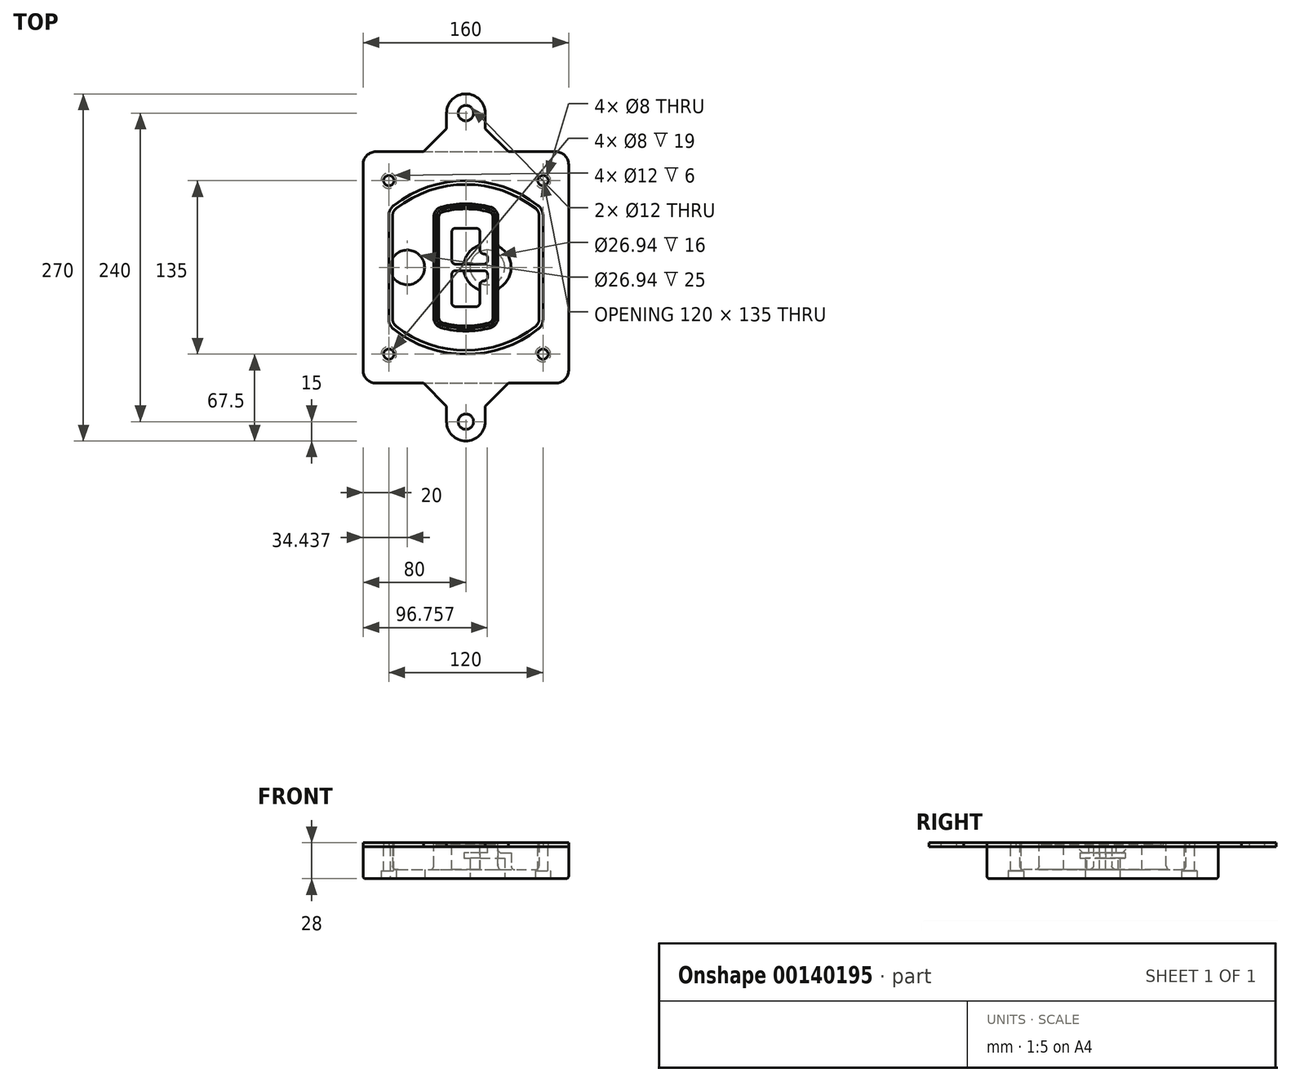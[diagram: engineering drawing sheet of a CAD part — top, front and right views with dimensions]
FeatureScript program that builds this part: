
annotation { "Feature Type Name" : "Feature", "Feature Type Description" : "" }
export const myFeature = defineFeature(function(context is Context, id is Id, definition is map)
    precondition{}
    {
        {
            var Q0;
            Q0=qCreatedBy(makeId("Top.planeOp"),FACE);
            var sketch = newSketch(context, id + "F0", { "sketchPlane" : qUnion([Q0])});
            skPoint(sketch, "E0.rect.middle", {"position": v(0, 0) * mm});
            skLineSegment(sketch, "E1.bottom", {"start": v(-70, -90) * mm, "end": v(70, -90) * mm});
            skLineSegment(sketch, "E1.top", {"start": v(-70, 90) * mm, "end": v(70, 90) * mm});
            skLineSegment(sketch, "E1.left", {"start": v(-80, -80) * mm, "end": v(-80, 80) * mm});
            skLineSegment(sketch, "E1.right", {"start": v(80, -80) * mm, "end": v(80, 80) * mm});
            skLineSegment(sketch, "E2", {"start": v(-80, 90) * mm, "end": v(80, -90) * mm, "construction": true});
            skLineSegment(sketch, "E3", {"start": v(80, 90) * mm, "end": v(-80, -90) * mm, "construction": true});
            skCircle(sketch, "E4", {"center": v(-60, 67.5) * mm, "radius": 4 * mm});
            skCircle(sketch, "E5", {"center": v(60, 67.5) * mm, "radius": 4 * mm});
            skCircle(sketch, "E6", {"center": v(60, -67.5) * mm, "radius": 4 * mm});
            skCircle(sketch, "E7", {"center": v(-60, -67.5) * mm, "radius": 4 * mm});
            skLineSegment(sketch, "E8", {"start": v(-60, 67.5) * mm, "end": v(60, 67.5) * mm, "construction": true});
            skLineSegment(sketch, "E9", {"start": v(60, 67.5) * mm, "end": v(60, -67.5) * mm, "construction": true});
            skLineSegment(sketch, "E10", {"start": v(60, -67.5) * mm, "end": v(-60, -67.5) * mm, "construction": true});
            skLineSegment(sketch, "E11", {"start": v(-60, -67.5) * mm, "end": v(-60, 67.5) * mm, "construction": true});
            skLineSegment(sketch, "E12", {"start": v(-60, 40.3) * mm, "end": v(-60, -40.3) * mm});
            skLineSegment(sketch, "E13", {"start": v(60, 40.3) * mm, "end": v(60, -40.3) * mm});
            skArc(sketch, "E14", {"start": v(56.15, 48.18) * mm, "mid": v(0, 67.5) * mm, "end": v(-56.15, 48.18) * mm});
            skArc(sketch, "E15", {"start": v(-56.15, -48.18) * mm, "mid": v(0, -67.5) * mm, "end": v(56.15, -48.18) * mm});
            skLineSegment(sketch, "E16", {"start": v(-60, 0) * mm, "end": v(60, 0) * mm, "construction": true});
            skPoint(sketch, "E17.visualSharp", {"position": v(-60, -45) * mm});
            skArc(sketch, "E17.filletArc", {"start": v(-60, -40.3) * mm, "mid": v(-58.99, -44.68) * mm, "end": v(-56.15, -48.18) * mm});
            skPoint(sketch, "E18.visualSharp", {"position": v(-60, 45) * mm});
            skArc(sketch, "E18.filletArc", {"start": v(-56.15, 48.18) * mm, "mid": v(-58.99, 44.68) * mm, "end": v(-60, 40.3) * mm});
            skPoint(sketch, "E19.visualSharp", {"position": v(60, 45) * mm});
            skArc(sketch, "E19.filletArc", {"start": v(60, 40.3) * mm, "mid": v(58.99, 44.68) * mm, "end": v(56.15, 48.18) * mm});
            skPoint(sketch, "E20.visualSharp", {"position": v(60, -45) * mm});
            skArc(sketch, "E20.filletArc", {"start": v(56.15, -48.18) * mm, "mid": v(58.99, -44.68) * mm, "end": v(60, -40.3) * mm});
            skPoint(sketch, "E21.visualSharp", {"position": v(-80, 90) * mm});
            skArc(sketch, "E21.filletArc", {"start": v(-70, 90) * mm, "mid": v(-77.07, 87.07) * mm, "end": v(-80, 80) * mm});
            skPoint(sketch, "E22.visualSharp", {"position": v(80, 90) * mm});
            skArc(sketch, "E22.filletArc", {"start": v(80, 80) * mm, "mid": v(77.07, 87.07) * mm, "end": v(70, 90) * mm});
            skPoint(sketch, "E23.visualSharp", {"position": v(80, -90) * mm});
            skArc(sketch, "E23.filletArc", {"start": v(70, -90) * mm, "mid": v(77.07, -87.07) * mm, "end": v(80, -80) * mm});
            skPoint(sketch, "E24.visualSharp", {"position": v(-80, -90) * mm});
            skArc(sketch, "E24.filletArc", {"start": v(-80, -80) * mm, "mid": v(-77.07, -87.07) * mm, "end": v(-70, -90) * mm});
            skArc(sketch, "E25.0", {"start": v(57, 40.3) * mm, "mid": v(56.3, 43.36) * mm, "end": v(54.3, 45.81) * mm});
            skLineSegment(sketch, "E25.1", {"start": v(57, 40.3) * mm, "end": v(57, -40.3) * mm});
            skArc(sketch, "E25.2", {"start": v(54.3, -45.81) * mm, "mid": v(56.3, -43.36) * mm, "end": v(57, -40.3) * mm});
            skArc(sketch, "E25.3", {"start": v(-54.3, -45.81) * mm, "mid": v(0, -64.5) * mm, "end": v(54.3, -45.81) * mm});
            skArc(sketch, "E25.4", {"start": v(-57, -40.3) * mm, "mid": v(-56.3, -43.36) * mm, "end": v(-54.3, -45.81) * mm});
            skArc(sketch, "E25.5", {"start": v(54.3, 45.81) * mm, "mid": v(0, 64.5) * mm, "end": v(-54.3, 45.81) * mm});
            skLineSegment(sketch, "E25.6", {"start": v(-57, 40.3) * mm, "end": v(-57, -40.3) * mm});
            skArc(sketch, "E25.7", {"start": v(-54.3, 45.81) * mm, "mid": v(-56.3, 43.36) * mm, "end": v(-57, 40.3) * mm});
            skArc(sketch, "E26.0", {"start": v(-58.62, 51.33) * mm, "mid": v(-62.58, 46.43) * mm, "end": v(-64, 40.3) * mm});
            skArc(sketch, "E26.1", {"start": v(58.62, 51.33) * mm, "mid": v(0, 71.5) * mm, "end": v(-58.62, 51.33) * mm});
            skArc(sketch, "E26.2", {"start": v(64, 40.3) * mm, "mid": v(62.58, 46.43) * mm, "end": v(58.62, 51.33) * mm});
            skLineSegment(sketch, "E26.3", {"start": v(64, 40.3) * mm, "end": v(64, -40.3) * mm});
            skArc(sketch, "E26.4", {"start": v(58.62, -51.33) * mm, "mid": v(62.58, -46.43) * mm, "end": v(64, -40.3) * mm});
            skLineSegment(sketch, "E26.5", {"start": v(-64, 40.3) * mm, "end": v(-64, -40.3) * mm});
            skArc(sketch, "E26.6", {"start": v(-58.62, -51.33) * mm, "mid": v(0, -71.5) * mm, "end": v(58.62, -51.33) * mm});
            skArc(sketch, "E26.7", {"start": v(-64, -40.3) * mm, "mid": v(-62.58, -46.43) * mm, "end": v(-58.62, -51.33) * mm});
            skSolve(sketch);
        }
        {
            var Q0;
            Q0=makeQuery(id+"F0.imprint","IMPRINT",FACE,{"disambiguationData":[TD([[makeQuery(id+"F0.imprint","IMPRINT",EDGE,{"derivedFrom":sQuery(id+"F0.wireOp",EDGE,"E1.bottom")}),1.0]])]});
            var Q1;
            Q1=makeQuery(id+"F0.imprint","IMPRINT",FACE,{"disambiguationData":[TD([[makeQuery(id+"F0.imprint","IMPRINT",EDGE,{"derivedFrom":sQuery(id+"F0.wireOp",EDGE,"E12")}),1.0]])]});
            var Q2;
            Q2=makeQuery(id+"F0.imprint","IMPRINT",FACE,{"disambiguationData":[TD([[makeQuery(id+"F0.imprint","IMPRINT",EDGE,{"derivedFrom":sQuery(id+"F0.wireOp",EDGE,"E25.0")}),1.0]])]});
            var Q3;
            Q3=makeQuery(id+"F0.imprint","IMPRINT",FACE,{"disambiguationData":[TD([[makeQuery(id+"F0.imprint","IMPRINT",EDGE,{"derivedFrom":sQuery(id+"F0.wireOp",EDGE,"E12")}),-1.0]])]});
            extrude(context, id + "F1", {"entities" : qUnion([Q0, Q1, Q2, Q3]), "oppositeDirection" : true, "depth" : 25 * mm});
        }
        {
            var Q0;
            Q0=makeQuery(id+"F0.imprint","IMPRINT",FACE,{"disambiguationData":[TD([[makeQuery(id+"F0.imprint","IMPRINT",EDGE,{"derivedFrom":sQuery(id+"F0.wireOp",EDGE,"E12")}),1.0]])]});
            extrude(context, id + "F2", {"entities" : qUnion([Q0]), "operationType" : NewBodyOperationType.ADD, "depth" : 3 * mm});
        }
        {
            var Q0;
            Q0=makeQuery(id+"F0.imprint","IMPRINT",FACE,{"disambiguationData":[TD([[makeQuery(id+"F0.imprint","IMPRINT",EDGE,{"derivedFrom":sQuery(id+"F0.wireOp",EDGE,"E25.0")}),1.0]])]});
            extrude(context, id + "F3", {"entities" : qUnion([Q0]), "operationType" : NewBodyOperationType.REMOVE, "oppositeDirection" : true, "depth" : 18 * mm});
        }
        {
            var Q0;
            Q0=makeQuery(id+"F2.opExtrude","CAP_FACE",FACE,{"disambiguationData":[OSD([sQuery(id+"F0.wireOp",EDGE,"E12"),sQuery(id+"F0.wireOp",EDGE,"E13"),sQuery(id+"F0.wireOp",EDGE,"E14"),sQuery(id+"F0.wireOp",EDGE,"E15"),sQuery(id+"F0.wireOp",EDGE,"E17.filletArc"),sQuery(id+"F0.wireOp",EDGE,"E18.filletArc"),sQuery(id+"F0.wireOp",EDGE,"E19.filletArc"),sQuery(id+"F0.wireOp",EDGE,"E20.filletArc"),sQuery(id+"F0.wireOp",EDGE,"E25.0"),sQuery(id+"F0.wireOp",EDGE,"E25.1"),sQuery(id+"F0.wireOp",EDGE,"E25.2"),sQuery(id+"F0.wireOp",EDGE,"E25.3"),sQuery(id+"F0.wireOp",EDGE,"E25.4"),sQuery(id+"F0.wireOp",EDGE,"E25.5"),sQuery(id+"F0.wireOp",EDGE,"E25.6"),sQuery(id+"F0.wireOp",EDGE,"E25.7")])],"isStart":false});
            var sketch = newSketch(context, id + "F4", { "sketchPlane" : qUnion([Q0])});
            skArc(sketch, "E27.0", {"start": v(-19.08, -46.97) * mm, "mid": v(0, -49.5) * mm, "end": v(19.08, -46.97) * mm});
            skArc(sketch, "E28.0", {"start": v(19.08, 46.97) * mm, "mid": v(0, 49.5) * mm, "end": v(-19.08, 46.97) * mm});
            skLineSegment(sketch, "E29", {"start": v(-25, 39.25) * mm, "end": v(-25, -39.25) * mm});
            skLineSegment(sketch, "E30", {"start": v(25, 39.25) * mm, "end": v(25, -39.25) * mm});
            skLineSegment(sketch, "E31", {"start": v(-25, 45.1) * mm, "end": v(25, 45.1) * mm, "construction": true});
            skLineSegment(sketch, "E32", {"start": v(-25, -45.1) * mm, "end": v(25, -45.1) * mm, "construction": true});
            skPoint(sketch, "E33.visualSharp", {"position": v(-25, 45.1) * mm});
            skArc(sketch, "E33.filletArc", {"start": v(-19.08, 46.97) * mm, "mid": v(-23.35, 44.11) * mm, "end": v(-25, 39.25) * mm});
            skPoint(sketch, "E34.visualSharp", {"position": v(25, 45.1) * mm});
            skArc(sketch, "E34.filletArc", {"start": v(25, 39.25) * mm, "mid": v(23.35, 44.11) * mm, "end": v(19.08, 46.97) * mm});
            skPoint(sketch, "E35.visualSharp", {"position": v(25, -45.1) * mm});
            skArc(sketch, "E35.filletArc", {"start": v(19.08, -46.97) * mm, "mid": v(23.35, -44.11) * mm, "end": v(25, -39.25) * mm});
            skPoint(sketch, "E36.visualSharp", {"position": v(-25, -45.1) * mm});
            skArc(sketch, "E36.filletArc", {"start": v(-25, -39.25) * mm, "mid": v(-23.35, -44.11) * mm, "end": v(-19.08, -46.97) * mm});
            skArc(sketch, "E37.0", {"start": v(54.3, 45.81) * mm, "mid": v(0, 64.5) * mm, "end": v(-54.3, 45.81) * mm});
            skArc(sketch, "E37.1", {"start": v(-54.3, 45.81) * mm, "mid": v(-56.3, 43.36) * mm, "end": v(-57, 40.3) * mm});
            skLineSegment(sketch, "E37.2", {"start": v(-57, 40.3) * mm, "end": v(-57, -40.3) * mm});
            skArc(sketch, "E37.3", {"start": v(-57, -40.3) * mm, "mid": v(-56.3, -43.36) * mm, "end": v(-54.3, -45.81) * mm});
            skArc(sketch, "E37.4", {"start": v(-54.3, -45.81) * mm, "mid": v(0, -64.5) * mm, "end": v(54.3, -45.81) * mm});
            skArc(sketch, "E37.5", {"start": v(54.3, -45.81) * mm, "mid": v(56.3, -43.36) * mm, "end": v(57, -40.3) * mm});
            skLineSegment(sketch, "E37.6", {"start": v(57, 40.3) * mm, "end": v(57, -40.3) * mm});
            skArc(sketch, "E37.7", {"start": v(57, 40.3) * mm, "mid": v(56.3, 43.36) * mm, "end": v(54.3, 45.81) * mm});
            skLineSegment(sketch, "E38.0", {"start": v(23, 39.25) * mm, "end": v(23, -39.25) * mm});
            skArc(sketch, "E38.1", {"start": v(18.56, -45.04) * mm, "mid": v(21.76, -42.9) * mm, "end": v(23, -39.25) * mm});
            skArc(sketch, "E38.2", {"start": v(-18.56, -45.04) * mm, "mid": v(0, -47.5) * mm, "end": v(18.56, -45.04) * mm});
            skArc(sketch, "E38.3", {"start": v(-23, -39.25) * mm, "mid": v(-21.76, -42.9) * mm, "end": v(-18.56, -45.04) * mm});
            skLineSegment(sketch, "E38.4", {"start": v(-23, 39.25) * mm, "end": v(-23, -39.25) * mm});
            skArc(sketch, "E38.5", {"start": v(23, 39.25) * mm, "mid": v(21.76, 42.9) * mm, "end": v(18.56, 45.04) * mm});
            skArc(sketch, "E38.6", {"start": v(-18.56, 45.04) * mm, "mid": v(-21.76, 42.9) * mm, "end": v(-23, 39.25) * mm});
            skArc(sketch, "E38.7", {"start": v(18.56, 45.04) * mm, "mid": v(0, 47.5) * mm, "end": v(-18.56, 45.04) * mm});
            skArc(sketch, "E39.0", {"start": v(21, 39.25) * mm, "mid": v(20.18, 41.68) * mm, "end": v(18.04, 43.1) * mm});
            skLineSegment(sketch, "E39.1", {"start": v(21, 39.25) * mm, "end": v(21, -39.25) * mm});
            skArc(sketch, "E39.2", {"start": v(18.04, -43.1) * mm, "mid": v(20.18, -41.68) * mm, "end": v(21, -39.25) * mm});
            skArc(sketch, "E39.3", {"start": v(-18.04, -43.1) * mm, "mid": v(0, -45.5) * mm, "end": v(18.04, -43.1) * mm});
            skArc(sketch, "E39.4", {"start": v(-21, -39.25) * mm, "mid": v(-20.18, -41.68) * mm, "end": v(-18.04, -43.1) * mm});
            skArc(sketch, "E39.5", {"start": v(18.04, 43.1) * mm, "mid": v(0, 45.5) * mm, "end": v(-18.04, 43.1) * mm});
            skLineSegment(sketch, "E39.6", {"start": v(-21, 39.25) * mm, "end": v(-21, -39.25) * mm});
            skArc(sketch, "E39.7", {"start": v(-18.04, 43.1) * mm, "mid": v(-20.18, 41.68) * mm, "end": v(-21, 39.25) * mm});
            skLineSegment(sketch, "E40", {"start": v(-25, 0) * mm, "end": v(25, 0) * mm, "construction": true});
            skLineSegment(sketch, "E41", {"start": v(-11, 5.5) * mm, "end": v(-11, 27.5) * mm});
            skLineSegment(sketch, "E42", {"start": v(-8, 30.5) * mm, "end": v(8, 30.5) * mm});
            skLineSegment(sketch, "E43", {"start": v(11, 27.5) * mm, "end": v(11, 13.5) * mm});
            skLineSegment(sketch, "E44", {"start": v(14, 10.5) * mm, "end": v(14, 10.5) * mm});
            skLineSegment(sketch, "E45", {"start": v(17, 7.5) * mm, "end": v(17, 5.5) * mm});
            skLineSegment(sketch, "E46", {"start": v(14, 2.5) * mm, "end": v(-8, 2.5) * mm});
            skPoint(sketch, "E47.visualSharp", {"position": v(-11, 30.5) * mm});
            skArc(sketch, "E47.filletArc", {"start": v(-8, 30.5) * mm, "mid": v(-10.12, 29.62) * mm, "end": v(-11, 27.5) * mm});
            skPoint(sketch, "E48.visualSharp", {"position": v(11, 30.5) * mm});
            skArc(sketch, "E48.filletArc", {"start": v(11, 27.5) * mm, "mid": v(10.12, 29.62) * mm, "end": v(8, 30.5) * mm});
            skPoint(sketch, "E49.visualSharp", {"position": v(11, 10.5) * mm});
            skArc(sketch, "E49.filletArc", {"start": v(11, 13.5) * mm, "mid": v(11.88, 11.38) * mm, "end": v(14, 10.5) * mm});
            skPoint(sketch, "E50.visualSharp", {"position": v(17, 10.5) * mm});
            skArc(sketch, "E50.filletArc", {"start": v(17, 7.5) * mm, "mid": v(16.12, 9.62) * mm, "end": v(14, 10.5) * mm});
            skPoint(sketch, "E51.visualSharp", {"position": v(17, 2.5) * mm});
            skArc(sketch, "E51.filletArc", {"start": v(14, 2.5) * mm, "mid": v(16.12, 3.38) * mm, "end": v(17, 5.5) * mm});
            skPoint(sketch, "E52.visualSharp", {"position": v(-11, 2.5) * mm});
            skArc(sketch, "E52.filletArc", {"start": v(-11, 5.5) * mm, "mid": v(-10.12, 3.38) * mm, "end": v(-8, 2.5) * mm});
            skLineSegment(sketch, "E53.0.MirrorCS", {"start": v(14, -2.5) * mm, "end": v(-8, -2.5) * mm});
            skArc(sketch, "E54.0.MirrorCS", {"start": v(-11, -5.5) * mm, "mid": v(-10.12, -3.38) * mm, "end": v(-8, -2.5) * mm});
            skLineSegment(sketch, "E55.0.MirrorCS", {"start": v(-11, -5.5) * mm, "end": v(-11, -27.5) * mm});
            skArc(sketch, "E56.0.MirrorCS", {"start": v(-8, -30.5) * mm, "mid": v(-10.12, -29.62) * mm, "end": v(-11, -27.5) * mm});
            skLineSegment(sketch, "E57.0.MirrorCS", {"start": v(-8, -30.5) * mm, "end": v(8, -30.5) * mm});
            skArc(sketch, "E58.0.MirrorCS", {"start": v(11, -27.5) * mm, "mid": v(10.12, -29.62) * mm, "end": v(8, -30.5) * mm});
            skLineSegment(sketch, "E59.0.MirrorCS", {"start": v(11, -27.5) * mm, "end": v(11, -13.5) * mm});
            skArc(sketch, "E60.0.MirrorCS", {"start": v(11, -13.5) * mm, "mid": v(11.88, -11.38) * mm, "end": v(14, -10.5) * mm});
            skArc(sketch, "E61.0.MirrorCS", {"start": v(17, -7.5) * mm, "mid": v(16.12, -9.62) * mm, "end": v(14, -10.5) * mm});
            skLineSegment(sketch, "E62.0.MirrorCS", {"start": v(17, -7.5) * mm, "end": v(17, -5.5) * mm});
            skArc(sketch, "E63.0.MirrorCS", {"start": v(14, -2.5) * mm, "mid": v(16.12, -3.38) * mm, "end": v(17, -5.5) * mm});
            skSolve(sketch);
        }
        {
            var Q0;
            Q0=makeQuery(id+"F4.imprint","IMPRINT",FACE,{"disambiguationData":[TD([[makeQuery(id+"F4.imprint","IMPRINT",EDGE,{"derivedFrom":sQuery(id+"F4.wireOp",EDGE,"E27.0")}),1.0]])]});
            var Q1;
            Q1=makeQuery(id+"F4.imprint","IMPRINT",FACE,{"disambiguationData":[TD([[makeQuery(id+"F4.imprint","IMPRINT",EDGE,{"derivedFrom":sQuery(id+"F4.wireOp",EDGE,"E38.0")}),-1.0]])]});
            var Q2;
            Q2=makeQuery(id+"F4.imprint","IMPRINT",FACE,{"disambiguationData":[TD([[makeQuery(id+"F4.imprint","IMPRINT",EDGE,{"derivedFrom":sQuery(id+"F4.wireOp",EDGE,"E39.0")}),1.0]])]});
            extrude(context, id + "F5", {"entities" : qUnion([Q0, Q1, Q2]), "operationType" : NewBodyOperationType.ADD, "endBound" : BoundingType.UP_TO_NEXT, "oppositeDirection" : true, "depth" : 25 * mm});
        }
        {
            var Q0;
            Q0=makeQuery(id+"F4.imprint","IMPRINT",FACE,{"disambiguationData":[TD([[makeQuery(id+"F4.imprint","IMPRINT",EDGE,{"derivedFrom":sQuery(id+"F4.wireOp",EDGE,"E38.0")}),-1.0]])]});
            extrude(context, id + "F6", {"entities" : qUnion([Q0]), "operationType" : NewBodyOperationType.REMOVE, "oppositeDirection" : true, "depth" : 2 * mm});
        }
        {
            var Q0;
            Q0=makeQuery(id+"F1.opExtrude","CAP_FACE",FACE,{"disambiguationData":[OSD([sQuery(id+"F0.wireOp",EDGE,"E1.bottom"),sQuery(id+"F0.wireOp",EDGE,"E1.top"),sQuery(id+"F0.wireOp",EDGE,"E1.left"),sQuery(id+"F0.wireOp",EDGE,"E1.right"),sQuery(id+"F0.wireOp",EDGE,"E4"),sQuery(id+"F0.wireOp",EDGE,"E5"),sQuery(id+"F0.wireOp",EDGE,"E6"),sQuery(id+"F0.wireOp",EDGE,"E7"),sQuery(id+"F0.wireOp",EDGE,"E21.filletArc"),sQuery(id+"F0.wireOp",EDGE,"E22.filletArc"),sQuery(id+"F0.wireOp",EDGE,"E23.filletArc"),sQuery(id+"F0.wireOp",EDGE,"E24.filletArc")])],"isStart":false});
            var sketch = newSketch(context, id + "F7", { "sketchPlane" : qUnion([Q0])});
            skCircle(sketch, "E64", {"center": v(16.76, 0) * mm, "radius": 13.47 * mm});
            skCircle(sketch, "E65", {"center": v(-45.56, 0) * mm, "radius": 13.47 * mm});
            skLineSegment(sketch, "E66", {"start": v(80, 0) * mm, "end": v(-80, 0) * mm});
            skCircle(sketch, "E67", {"center": v(16.76, 0) * mm, "radius": 18.47 * mm});
            skCircle(sketch, "E68", {"center": v(60, -67.5) * mm, "radius": 6 * mm});
            skCircle(sketch, "E69", {"center": v(-60, -67.5) * mm, "radius": 6 * mm});
            skCircle(sketch, "E70", {"center": v(-60, 67.5) * mm, "radius": 6 * mm});
            skCircle(sketch, "E71", {"center": v(60, 67.5) * mm, "radius": 6 * mm});
            skSolve(sketch);
        }
        {
            var Q0;
            {var subQ1=sQuery(id+"F7.wireOp",EDGE,"E66");var subQ4=sQuery(id+"F7.wireOp",EDGE,"E64");var subQ6=makeQuery(id+"F7.imprint","INTERSECT",VERTEX,{"disambiguationData":[OD(0.0)],"derivedFrom":[subQ4,subQ1]});Q0=makeQuery(id+"F7.imprint","IMPRINT",FACE,{"disambiguationData":[TD([[makeQuery(id+"F7.imprint","IMPRINT",EDGE,{"disambiguationData":[TD([[subQ6,-1.0]])],"derivedFrom":subQ4}),-1.0]])]});}
            var Q1;
            {var subQ0=sQuery(id+"F7.wireOp",EDGE,"E66");var subQ1=sQuery(id+"F7.wireOp",EDGE,"E64");var subQ3=makeQuery(id+"F7.imprint","INTERSECT",VERTEX,{"disambiguationData":[OD(0.0)],"derivedFrom":[subQ1,subQ0]});Q1=makeQuery(id+"F7.imprint","IMPRINT",FACE,{"disambiguationData":[TD([[makeQuery(id+"F7.imprint","IMPRINT",EDGE,{"disambiguationData":[TD([[subQ3,-1.0]])],"derivedFrom":subQ1}),1.0]])]});}
            var Q2;
            {var subQ0=sQuery(id+"F7.wireOp",EDGE,"E66");var subQ1=sQuery(id+"F7.wireOp",EDGE,"E64");var subQ3=makeQuery(id+"F7.imprint","INTERSECT",VERTEX,{"disambiguationData":[OD(0.0)],"derivedFrom":[subQ1,subQ0]});Q2=makeQuery(id+"F7.imprint","IMPRINT",FACE,{"disambiguationData":[TD([[makeQuery(id+"F7.imprint","IMPRINT",EDGE,{"disambiguationData":[TD([[subQ3,1.0]])],"derivedFrom":subQ1}),1.0]])]});}
            var Q3;
            {var subQ1=sQuery(id+"F7.wireOp",EDGE,"E66");var subQ4=sQuery(id+"F7.wireOp",EDGE,"E64");var subQ6=makeQuery(id+"F7.imprint","INTERSECT",VERTEX,{"disambiguationData":[OD(0.0)],"derivedFrom":[subQ4,subQ1]});Q3=makeQuery(id+"F7.imprint","IMPRINT",FACE,{"disambiguationData":[TD([[makeQuery(id+"F7.imprint","IMPRINT",EDGE,{"disambiguationData":[TD([[subQ6,1.0]])],"derivedFrom":subQ4}),-1.0]])]});}
            extrude(context, id + "F8", {"entities" : qUnion([Q0, Q1, Q2, Q3]), "operationType" : NewBodyOperationType.ADD, "oppositeDirection" : true, "depth" : 20 * mm});
        }
        {
            var Q0;
            {var subQ0=sQuery(id+"F7.wireOp",EDGE,"E66");var subQ1=sQuery(id+"F7.wireOp",EDGE,"E64");var subQ3=makeQuery(id+"F7.imprint","INTERSECT",VERTEX,{"disambiguationData":[OD(0.0)],"derivedFrom":[subQ1,subQ0]});Q0=makeQuery(id+"F7.imprint","IMPRINT",FACE,{"disambiguationData":[TD([[makeQuery(id+"F7.imprint","IMPRINT",EDGE,{"disambiguationData":[TD([[subQ3,-1.0]])],"derivedFrom":subQ1}),1.0]])]});}
            var Q1;
            {var subQ0=sQuery(id+"F7.wireOp",EDGE,"E66");var subQ1=sQuery(id+"F7.wireOp",EDGE,"E64");var subQ3=makeQuery(id+"F7.imprint","INTERSECT",VERTEX,{"disambiguationData":[OD(0.0)],"derivedFrom":[subQ1,subQ0]});Q1=makeQuery(id+"F7.imprint","IMPRINT",FACE,{"disambiguationData":[TD([[makeQuery(id+"F7.imprint","IMPRINT",EDGE,{"disambiguationData":[TD([[subQ3,1.0]])],"derivedFrom":subQ1}),1.0]])]});}
            extrude(context, id + "F9", {"entities" : qUnion([Q0, Q1]), "operationType" : NewBodyOperationType.REMOVE, "oppositeDirection" : true, "depth" : 16 * mm});
        }
        {
            var Q0;
            {var subQ0=sQuery(id+"F7.wireOp",EDGE,"E66");var subQ1=sQuery(id+"F7.wireOp",EDGE,"E65");var subQ3=makeQuery(id+"F7.imprint","INTERSECT",VERTEX,{"disambiguationData":[OD(0.0)],"derivedFrom":[subQ1,subQ0]});Q0=makeQuery(id+"F7.imprint","IMPRINT",FACE,{"disambiguationData":[TD([[makeQuery(id+"F7.imprint","IMPRINT",EDGE,{"disambiguationData":[TD([[subQ3,-1.0]])],"derivedFrom":subQ1}),1.0]])]});}
            var Q1;
            {var subQ0=sQuery(id+"F7.wireOp",EDGE,"E66");var subQ1=sQuery(id+"F7.wireOp",EDGE,"E65");var subQ3=makeQuery(id+"F7.imprint","INTERSECT",VERTEX,{"disambiguationData":[OD(0.0)],"derivedFrom":[subQ1,subQ0]});Q1=makeQuery(id+"F7.imprint","IMPRINT",FACE,{"disambiguationData":[TD([[makeQuery(id+"F7.imprint","IMPRINT",EDGE,{"disambiguationData":[TD([[subQ3,1.0]])],"derivedFrom":subQ1}),1.0]])]});}
            extrude(context, id + "F10", {"entities" : qUnion([Q0, Q1]), "operationType" : NewBodyOperationType.REMOVE, "oppositeDirection" : true, "depth" : 25 * mm});
        }
        {
            var Q0;
            Q0=makeQuery(id+"F7.imprint","IMPRINT",FACE,{"disambiguationData":[TD([[makeQuery(id+"F7.imprint","IMPRINT",EDGE,{"derivedFrom":sQuery(id+"F7.wireOp",EDGE,"E68")}),1.0]])]});
            var Q1;
            Q1=makeQuery(id+"F7.imprint","IMPRINT",FACE,{"disambiguationData":[TD([[makeQuery(id+"F7.imprint","IMPRINT",EDGE,{"derivedFrom":makeQuery(id+"F1.opExtrude","CAP_EDGE",EDGE,{"disambiguationData":[OSD([sQuery(id+"F0.wireOp",EDGE,"E5")])],"isStart":false})}),-1.0]])]});
            var Q2;
            Q2=makeQuery(id+"F7.imprint","IMPRINT",FACE,{"disambiguationData":[TD([[makeQuery(id+"F7.imprint","IMPRINT",EDGE,{"derivedFrom":sQuery(id+"F7.wireOp",EDGE,"E69")}),1.0]])]});
            var Q3;
            Q3=makeQuery(id+"F7.imprint","IMPRINT",FACE,{"disambiguationData":[TD([[makeQuery(id+"F7.imprint","IMPRINT",EDGE,{"derivedFrom":makeQuery(id+"F1.opExtrude","CAP_EDGE",EDGE,{"disambiguationData":[OSD([sQuery(id+"F0.wireOp",EDGE,"E4")])],"isStart":false})}),-1.0]])]});
            var Q4;
            Q4=makeQuery(id+"F7.imprint","IMPRINT",FACE,{"disambiguationData":[TD([[makeQuery(id+"F7.imprint","IMPRINT",EDGE,{"derivedFrom":sQuery(id+"F7.wireOp",EDGE,"E70")}),1.0]])]});
            var Q5;
            Q5=makeQuery(id+"F7.imprint","IMPRINT",FACE,{"disambiguationData":[TD([[makeQuery(id+"F7.imprint","IMPRINT",EDGE,{"derivedFrom":makeQuery(id+"F1.opExtrude","CAP_EDGE",EDGE,{"disambiguationData":[OSD([sQuery(id+"F0.wireOp",EDGE,"E7")])],"isStart":false})}),-1.0]])]});
            var Q6;
            Q6=makeQuery(id+"F7.imprint","IMPRINT",FACE,{"disambiguationData":[TD([[makeQuery(id+"F7.imprint","IMPRINT",EDGE,{"derivedFrom":sQuery(id+"F7.wireOp",EDGE,"E71")}),1.0]])]});
            var Q7;
            Q7=makeQuery(id+"F7.imprint","IMPRINT",FACE,{"disambiguationData":[TD([[makeQuery(id+"F7.imprint","IMPRINT",EDGE,{"derivedFrom":makeQuery(id+"F1.opExtrude","CAP_EDGE",EDGE,{"disambiguationData":[OSD([sQuery(id+"F0.wireOp",EDGE,"E6")])],"isStart":false})}),-1.0]])]});
            extrude(context, id + "F11", {"entities" : qUnion([Q0, Q1, Q2, Q3, Q4, Q5, Q6, Q7]), "operationType" : NewBodyOperationType.REMOVE, "oppositeDirection" : true, "depth" : 6 * mm});
        }
        {
            var Q0;
            Q0=makeQuery(id+"F9.boolean.opBoolean","COPY",FACE,{"derivedFrom":makeQuery(id+"F9.opExtrude","CAP_FACE",FACE,{"disambiguationData":[OSD([sQuery(id+"F7.wireOp",EDGE,"E64")])],"isStart":false})});
            var sketch = newSketch(context, id + "F12", { "sketchPlane" : qUnion([Q0])});
            skArc(sketch, "E72.0", {"start": v(11, 17.55) * mm, "mid": v(2.57, 11.82) * mm, "end": v(-1.54, 2.5) * mm});
            skArc(sketch, "E72.1", {"start": v(-1.54, -2.5) * mm, "mid": v(2.57, -11.82) * mm, "end": v(11, -17.55) * mm});
            skLineSegment(sketch, "E73", {"start": v(-1.54, -2.5) * mm, "end": v(14, -2.5) * mm});
            skLineSegment(sketch, "E74.0", {"start": v(14, 2.5) * mm, "end": v(-1.54, 2.5) * mm});
            skArc(sketch, "E74.1", {"start": v(14, 2.5) * mm, "mid": v(16.12, 3.38) * mm, "end": v(17, 5.5) * mm});
            skLineSegment(sketch, "E74.2", {"start": v(17, 7.5) * mm, "end": v(17, 5.5) * mm});
            skArc(sketch, "E74.3", {"start": v(17, 7.5) * mm, "mid": v(16.12, 9.62) * mm, "end": v(14, 10.5) * mm});
            skArc(sketch, "E74.4", {"start": v(11, 13.5) * mm, "mid": v(11.88, 11.38) * mm, "end": v(14, 10.5) * mm});
            skLineSegment(sketch, "E74.5", {"start": v(11, 17.55) * mm, "end": v(11, 13.5) * mm});
            skLineSegment(sketch, "E74.7", {"start": v(14, -2.5) * mm, "end": v(-1.54, -2.5) * mm});
            skArc(sketch, "E74.8", {"start": v(14, -2.5) * mm, "mid": v(16.12, -3.38) * mm, "end": v(17, -5.5) * mm});
            skLineSegment(sketch, "E74.9", {"start": v(17, -7.5) * mm, "end": v(17, -5.5) * mm});
            skArc(sketch, "E74.10", {"start": v(17, -7.5) * mm, "mid": v(16.12, -9.62) * mm, "end": v(14, -10.5) * mm});
            skArc(sketch, "E74.11", {"start": v(11, -13.5) * mm, "mid": v(11.88, -11.38) * mm, "end": v(14, -10.5) * mm});
            skLineSegment(sketch, "E74.12", {"start": v(11, -17.55) * mm, "end": v(11, -13.5) * mm});
            skPoint(sketch, "E75.orphan", {"position": v(11, -27.5) * mm});
            skPoint(sketch, "E76.orphan", {"position": v(-8, -2.5) * mm});
            skPoint(sketch, "E77.orphan", {"position": v(-8, 2.5) * mm});
            skPoint(sketch, "E78.orphan", {"position": v(11, 27.5) * mm});
            skSolve(sketch);
        }
        {
            var Q0;
            {var subQ7=sQuery(id+"F12.wireOp",EDGE,"E72.0");var subQ14=sQuery(id+"F12.wireOp",EDGE,"E72.1");var subQ16=sQuery(id+"F12.wireOp",EDGE,"E74.1");var subQ18=sQuery(id+"F12.wireOp",EDGE,"E74.8");Q0=qUnion([makeQuery(id+"F12.imprint","IMPRINT",FACE,{"disambiguationData":[TD([[makeQuery(id+"F12.imprint","IMPRINT",EDGE,{"derivedFrom":subQ7}),1.0]])]}),makeQuery(id+"F12.imprint","IMPRINT",FACE,{"disambiguationData":[TD([[makeQuery(id+"F12.imprint","IMPRINT",EDGE,{"derivedFrom":subQ14}),1.0]])]}),makeQuery(id+"F12.imprint","IMPRINT",FACE,{"disambiguationData":[TD([[makeQuery(id+"F12.imprint","IMPRINT",EDGE,{"derivedFrom":subQ16}),1.0]])]}),makeQuery(id+"F12.imprint","IMPRINT",FACE,{"disambiguationData":[TD([[makeQuery(id+"F12.imprint","IMPRINT",EDGE,{"derivedFrom":subQ18}),-1.0]])]})]);}
            var Q1;
            Q1=makeQuery(id+"F5.boolean.opBoolean","SPLIT",FACE,{"disambiguationData":[TD([makeQuery(id+"F5.opExtrude","SWEPT_FACE",FACE,{"disambiguationData":[OSD([sQuery(id+"F4.wireOp",EDGE,"E41")])]})])],"derivedFrom":makeQuery(id+"F3.boolean.opBoolean","COPY",FACE,{"derivedFrom":makeQuery(id+"F3.opExtrude","CAP_FACE",FACE,{"disambiguationData":[OSD([sQuery(id+"F0.wireOp",EDGE,"E25.0"),sQuery(id+"F0.wireOp",EDGE,"E25.1"),sQuery(id+"F0.wireOp",EDGE,"E25.2"),sQuery(id+"F0.wireOp",EDGE,"E25.3"),sQuery(id+"F0.wireOp",EDGE,"E25.4"),sQuery(id+"F0.wireOp",EDGE,"E25.5"),sQuery(id+"F0.wireOp",EDGE,"E25.6"),sQuery(id+"F0.wireOp",EDGE,"E25.7")])],"isStart":false})})});
            extrude(context, id + "F13", {"entities" : qUnion([Q0]), "operationType" : NewBodyOperationType.REMOVE, "endBound" : BoundingType.UP_TO_SURFACE, "endBoundEntityFace" : qUnion([Q1]), "depth" : 25 * mm});
        }
        {
            var Q0;
            Q0=makeQuery(id+"F3.boolean.opBoolean","COPY",EDGE,{"derivedFrom":makeQuery(id+"F3.opExtrude","CAP_EDGE",EDGE,{"disambiguationData":[OSD([sQuery(id+"F0.wireOp",EDGE,"E25.6")])],"isStart":false})});
            var Q1;
            Q1=makeQuery(id+"F8.boolean.opBoolean","INTERSECT",EDGE,{"derivedFrom":[makeQuery(id+"F5.opExtrude","SWEPT_FACE",FACE,{"disambiguationData":[OSD([sQuery(id+"F4.wireOp",EDGE,"E30")])]}),makeQuery(id+"F8.opExtrude","CAP_FACE",FACE,{"disambiguationData":[OSD([sQuery(id+"F7.wireOp",EDGE,"E67")])],"isStart":false})]});
            var Q2;
            Q2=makeQuery(id+"F8.boolean.opBoolean","INTERSECT",EDGE,{"disambiguationData":[OD(1.0)],"derivedFrom":[makeQuery(id+"F5.opExtrude","SWEPT_FACE",FACE,{"disambiguationData":[OSD([sQuery(id+"F4.wireOp",EDGE,"E30")])]}),makeQuery(id+"F8.opExtrude","SWEPT_FACE",FACE,{"disambiguationData":[OSD([sQuery(id+"F7.wireOp",EDGE,"E67")])]})]});
            var Q3;
            {var subQ0=sQuery(id+"F4.wireOp",EDGE,"E30");Q3=makeQuery(id+"F8.boolean.opBoolean","SPLIT",EDGE,{"disambiguationData":[TD([makeQuery(id+"F5.opExtrude","SWEPT_FACE",FACE,{"disambiguationData":[OSD([sQuery(id+"F4.wireOp",EDGE,"E35.filletArc")])]})])],"derivedFrom":makeQuery(id+"F5.opExtrude","CAP_EDGE",EDGE,{"disambiguationData":[OSD([subQ0])],"isStart":false})});}
            var Q4;
            {var subQ0=sQuery(id+"F0.wireOp",EDGE,"E25.7");var subQ1=sQuery(id+"F0.wireOp",EDGE,"E25.1");var subQ2=sQuery(id+"F0.wireOp",EDGE,"E25.6");var subQ3=sQuery(id+"F0.wireOp",EDGE,"E25.5");var subQ4=sQuery(id+"F0.wireOp",EDGE,"E25.4");var subQ5=sQuery(id+"F0.wireOp",EDGE,"E25.0");var subQ6=sQuery(id+"F0.wireOp",EDGE,"E25.2");var subQ7=sQuery(id+"F0.wireOp",EDGE,"E25.3");Q4=makeQuery(id+"F8.boolean.opBoolean","INTERSECT",EDGE,{"derivedFrom":[makeQuery(id+"F5.boolean.opBoolean","SPLIT",FACE,{"disambiguationData":[TD([makeQuery(id+"F2.opExtrude","SWEPT_FACE",FACE,{"disambiguationData":[OSD([subQ5])]})])],"derivedFrom":makeQuery(id+"F3.boolean.opBoolean","COPY",FACE,{"derivedFrom":makeQuery(id+"F3.opExtrude","CAP_FACE",FACE,{"disambiguationData":[OSD([subQ5,subQ1,subQ6,subQ7,subQ4,subQ3,subQ2,subQ0])],"isStart":false})})}),makeQuery(id+"F8.opExtrude","SWEPT_FACE",FACE,{"disambiguationData":[OSD([sQuery(id+"F7.wireOp",EDGE,"E67")])]})]});}
            var Q5;
            Q5=makeQuery(id+"F8.boolean.opBoolean","INTERSECT",EDGE,{"disambiguationData":[OD(0.0)],"derivedFrom":[makeQuery(id+"F5.opExtrude","SWEPT_FACE",FACE,{"disambiguationData":[OSD([sQuery(id+"F4.wireOp",EDGE,"E30")])]}),makeQuery(id+"F8.opExtrude","SWEPT_FACE",FACE,{"disambiguationData":[OSD([sQuery(id+"F7.wireOp",EDGE,"E67")])]})]});
            fillet(context, id + "F14", {"entities" : qUnion([Q0, Q1, Q2, Q3, Q4, Q5]), "radius" : 3 * mm, "tangentPropagation" : true, "allowEdgeOverflow" : false});
        }
        {
            var Q0;
            Q0=makeQuery(id+"F1.opExtrude","CAP_EDGE",EDGE,{"disambiguationData":[OSD([sQuery(id+"F0.wireOp",EDGE,"E1.bottom")])],"isStart":false});
            fillet(context, id + "F15", {"entities" : qUnion([Q0]), "radius" : 2 * mm, "tangentPropagation" : true, "allowEdgeOverflow" : false});
        }
        {
            var Q0;
            {var subQ0=sQuery(id+"F0.wireOp",EDGE,"E22.filletArc");var subQ1=sQuery(id+"F0.wireOp",EDGE,"E7");var subQ2=sQuery(id+"F0.wireOp",EDGE,"E6");var subQ3=sQuery(id+"F0.wireOp",EDGE,"E5");var subQ4=sQuery(id+"F0.wireOp",EDGE,"E4");var subQ5=sQuery(id+"F0.wireOp",EDGE,"E1.bottom");var subQ6=sQuery(id+"F0.wireOp",EDGE,"E21.filletArc");var subQ7=sQuery(id+"F0.wireOp",EDGE,"E1.top");var subQ8=sQuery(id+"F0.wireOp",EDGE,"E1.left");var subQ9=sQuery(id+"F0.wireOp",EDGE,"E1.right");var subQ10=sQuery(id+"F0.wireOp",EDGE,"E23.filletArc");var subQ11=sQuery(id+"F0.wireOp",EDGE,"E24.filletArc");Q0=makeQuery(id+"F2.boolean.opBoolean","SPLIT",FACE,{"disambiguationData":[TD([makeQuery(id+"F1.opExtrude","SWEPT_FACE",FACE,{"disambiguationData":[OSD([subQ5])]})])],"derivedFrom":makeQuery(id+"F1.opExtrude","CAP_FACE",FACE,{"disambiguationData":[OSD([subQ5,subQ7,subQ8,subQ9,subQ4,subQ3,subQ2,subQ1,subQ6,subQ0,subQ10,subQ11])],"isStart":true})});}
            var sketch = newSketch(context, id + "F16", { "sketchPlane" : qUnion([Q0])});
            skLineSegment(sketch, "E79", {"start": v(0, 90) * mm, "end": v(0, 120) * mm, "construction": true});
            skCircle(sketch, "E80", {"center": v(0, 120) * mm, "radius": 6 * mm});
            skArc(sketch, "E81", {"start": v(15, 120) * mm, "mid": v(0, 135) * mm, "end": v(-15, 120) * mm});
            skLineSegment(sketch, "E82", {"start": v(-15, 120) * mm, "end": v(-15, 108) * mm});
            skLineSegment(sketch, "E83", {"start": v(15, 120) * mm, "end": v(15, 108) * mm});
            skLineSegment(sketch, "E84", {"start": v(15, 108) * mm, "end": v(33, 90) * mm});
            skLineSegment(sketch, "E85", {"start": v(-15, 108) * mm, "end": v(-33, 90) * mm});
            skLineSegment(sketch, "E86", {"start": v(-80, 0) * mm, "end": v(80, 0) * mm, "construction": true});
            skLineSegment(sketch, "E87.MirrorCS", {"start": v(0, -90) * mm, "end": v(0, -120) * mm, "construction": true});
            skLineSegment(sketch, "E88.MirrorCS", {"start": v(15, -108) * mm, "end": v(33, -90) * mm});
            skLineSegment(sketch, "E89.MirrorCS", {"start": v(-15, -108) * mm, "end": v(-33, -90) * mm});
            skCircle(sketch, "E90.MirrorC", {"center": v(0, -120) * mm, "radius": 6 * mm});
            skLineSegment(sketch, "E91.MirrorCS", {"start": v(-15, -120) * mm, "end": v(-15, -108) * mm});
            skArc(sketch, "E92.MirrorCS", {"start": v(15, -120) * mm, "mid": v(0, -135) * mm, "end": v(-15, -120) * mm});
            skLineSegment(sketch, "E93.MirrorCS", {"start": v(15, -120) * mm, "end": v(15, -108) * mm});
            skSolve(sketch);
        }
        {
            var Q0;
            {var subQ0=sQuery(id+"F16.wireOp",EDGE,"E88.MirrorCS");Q0=makeQuery(id+"F16.imprint","IMPRINT",FACE,{"disambiguationData":[TD([[makeQuery(id+"F16.imprint","IMPRINT",EDGE,{"derivedFrom":subQ0}),1.0]])]});}
            var Q1;
            Q1=makeQuery(id+"F16.imprint","IMPRINT",FACE,{"disambiguationData":[TD([[makeQuery(id+"F16.imprint","IMPRINT",EDGE,{"derivedFrom":sQuery(id+"F16.wireOp",EDGE,"E80")}),-1.0]])]});
            var Q2;
            Q2=makeQuery(id+"F16.imprint","IMPRINT",FACE,{"disambiguationData":[TD([[makeQuery(id+"F16.imprint","IMPRINT",EDGE,{"derivedFrom":makeQuery(id+"F1.opExtrude","CAP_EDGE",EDGE,{"disambiguationData":[OSD([sQuery(id+"F0.wireOp",EDGE,"E1.left")])],"isStart":true})}),-1.0]])]});
            var Q3;
            Q3=makeQuery(id+"F2.opExtrude","CAP_FACE",FACE,{"disambiguationData":[OSD([sQuery(id+"F0.wireOp",EDGE,"E12"),sQuery(id+"F0.wireOp",EDGE,"E13"),sQuery(id+"F0.wireOp",EDGE,"E14"),sQuery(id+"F0.wireOp",EDGE,"E15"),sQuery(id+"F0.wireOp",EDGE,"E17.filletArc"),sQuery(id+"F0.wireOp",EDGE,"E18.filletArc"),sQuery(id+"F0.wireOp",EDGE,"E19.filletArc"),sQuery(id+"F0.wireOp",EDGE,"E20.filletArc"),sQuery(id+"F0.wireOp",EDGE,"E25.0"),sQuery(id+"F0.wireOp",EDGE,"E25.1"),sQuery(id+"F0.wireOp",EDGE,"E25.2"),sQuery(id+"F0.wireOp",EDGE,"E25.3"),sQuery(id+"F0.wireOp",EDGE,"E25.4"),sQuery(id+"F0.wireOp",EDGE,"E25.5"),sQuery(id+"F0.wireOp",EDGE,"E25.6"),sQuery(id+"F0.wireOp",EDGE,"E25.7")])],"isStart":false});
            extrude(context, id + "F17", {"entities" : qUnion([Q0, Q1, Q2]), "endBound" : BoundingType.UP_TO_SURFACE, "endBoundEntityFace" : qUnion([Q3]), "depth" : 25 * mm});
        }
    });
